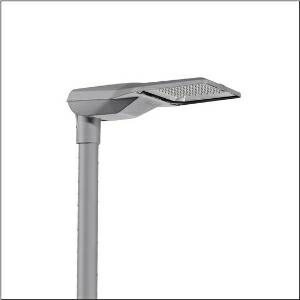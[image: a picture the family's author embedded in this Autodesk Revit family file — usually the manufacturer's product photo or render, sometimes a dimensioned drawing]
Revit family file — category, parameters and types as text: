
# Revit family: streetlight_sl_21_iq_midi___st0_5a_5xe3b31d08mb_db69
name_source: partatom
category: Lighting Fixtures
units: mm (PartAtom-declared; Revit-internal decimal feet)

## family parameters
Cut with Voids When Loaded = No
Host = Face
Light Source = No
Part Type = Normal
Room Calculation Point = No
Round Connector Dimension = Use Diameter
Shared = No

## types (1)
- --- (1 x LED, 19500 lm, 146.7 W, 3000K)
    Apparent Load = 147 VA
    CIE Flux Codes = 41 75 97 100 100
    Color Rendering = 70
    Color Temperature = 3000K
    Default Elevation = 1800 mm
    Description = Streetlight SL 21 iQ midi, mast luminaire, primary light control with lens, of PMMA, primary optical cover: cover, of toughened safety glass, transparent, light distribution: ST0.5a, light emission: direct distribution, primary light characteristic: asymmetric, installation type: post-top, side-entry, LED, High Power LED, rated luminous flux: 19.500lm, luminous efficacy: 133lm/W, light colour: 730, colour temperature: 3000K, control gear: iQ-Comfort, control: Auto-Match, Temp-Guard, Lumen-Switch, Night-Set, Smart-Wire, Light-Fading, Desk-Remote (wireless, voltage-free reading and setting of iQ features in the workshop via application-optimized NFC function/RFID function), optimised constant luminous flux control (CLO 2.0), pre-setting: linear dimming characteristic, mains connection: 230..240V, AC, 50/60Hz, start of lifetime: 147W, end of service life: 161W, reduction: 62W, luminaire housing, of diecast aluminium, powder-coated, Siteco® metallic grey (DB 702S), corrosivity category C5 mid according to DIN EN ISO 12944, please order mast flange separately, inclination adjustable: 0°, 5°, 10°, 15°, sealing non-destructively replaceable, multi-level sealing system, length: 644mm, width: 335mm, height: 110mm, mast flange for spigot size: 42mm (side-entry): 5XC10008XM4, 60/48mm (side-entry/post-top): 5XC10108XM2, 76/60mm (side-entry/post-top): 5XC10108XM1, mounting height: 4..8m, protection rating (complete): IP66, insulation class (complete): insulation class II (safety insulation), certification: CE, ENEC, ENEC+, VDE, impact resistance: IK10, permissible operating ambient temperature for outdoor applications: -40..+50°C, standard-compliant lighting for roads and squares, packaging unit: 1 piece

Light Distribution: ST0.5a
    Height = 111 mm
    Lamp = 1 x LED
    Lamp Light Flux = 19500 lm
    Lamp Power = 146.7 W
    Lamp count = 1
    Length = 644 mm
    Luminous efficacy = 133 lm/W
    Manufacturer = Siteco
    ModVariant = No
    Model = 5XE3B31D08MB
    Number of Poles = 1
    OnlyDefault = Yes
    Power Factor = 1
    Product Name = Streetlight SL 21 iQ midi | ST0.5a
    Product group = mast luminaire | pylon top
    ProductGroupID = 6100
    Protection Class = Protection class II
    Protection Degree = IP 66
    RLX_Detail_Level = 1
    RLX_Emergency_Light_Flux = 0 lm
    RLX_Emergency_Type = 0
    RLX_Emergency_Type_DB = No
    RlxData = <blob elided: 37945 chars, md5=96cb829e>
    Socket = socket
    Standby Power = 0 W
    System Light Flux = 19499 lm
    System Power = 147 W
    Type Comments = factory setting: luminous flux: 100 % | dim-lin: 254 | 753 mA
    Type Image = l_1004298.jpg
    URL = http://relux.com
    VarID = @adj_213173
    Voltage = 0 V
    Weight = 0.00 kg
    Width = 336 mm

## geometry (parser evidence)
native form markers: Blend x4, Sweep x11
no freeform markers — native parametric forms only
